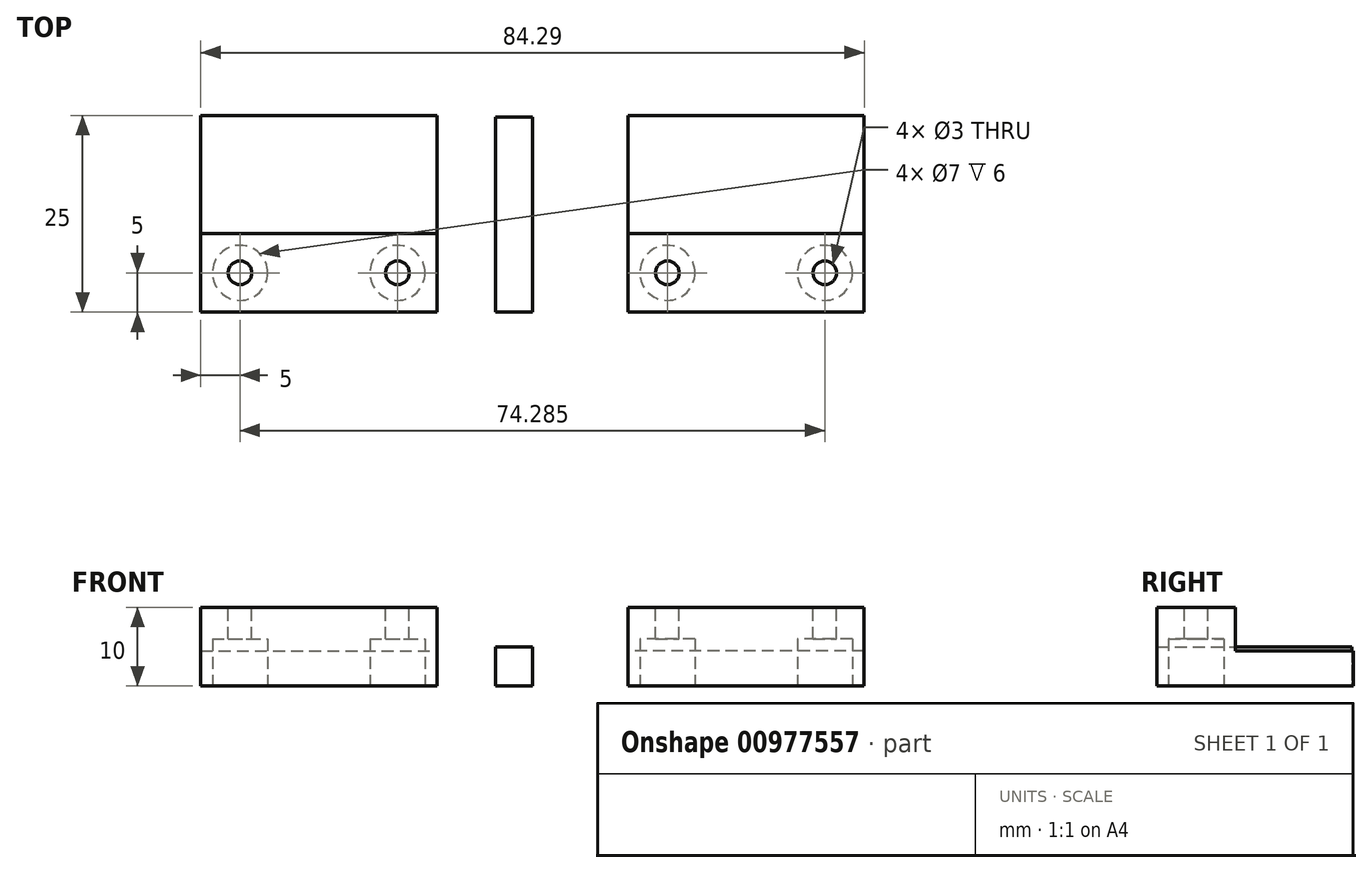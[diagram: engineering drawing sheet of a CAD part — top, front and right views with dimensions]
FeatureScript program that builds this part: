
annotation { "Feature Type Name" : "Feature", "Feature Type Description" : "" }
export const myFeature = defineFeature(function(context is Context, id is Id, definition is map)
    precondition{}
    {
        {
            var Q0;
            Q0=qCreatedBy(makeId("Top.planeOp"),FACE);
            var sketch = newSketch(context, id + "F0", { "sketchPlane" : qUnion([Q0])});
            skLineSegment(sketch, "E0.bottom", {"start": v(-15, -12.5) * mm, "end": v(15, -12.5) * mm});
            skLineSegment(sketch, "E0.top", {"start": v(-15, 12.5) * mm, "end": v(15, 12.5) * mm});
            skLineSegment(sketch, "E0.left", {"start": v(-15, -12.5) * mm, "end": v(-15, 12.5) * mm});
            skLineSegment(sketch, "E0.right", {"start": v(15, -12.5) * mm, "end": v(15, 12.5) * mm});
            skPoint(sketch, "E0.middle", {"position": v(0, 0) * mm});
            skSolve(sketch);
        }
        {
            var Q0;
            Q0=qSketchRegion(id+"F0",true);
            extrude(context, id + "F1", {"entities" : qUnion([Q0]), "depth" : 10 * mm, "offsetDistance" : 25 * mm});
        }
        {
            var Q0;
            Q0=makeQuery(id+"F1.opExtrude","CAP_FACE",FACE,{"disambiguationData":[OSD([sQuery(id+"F0.wireOp",EDGE,"E0.bottom"),sQuery(id+"F0.wireOp",EDGE,"E0.top"),sQuery(id+"F0.wireOp",EDGE,"E0.left"),sQuery(id+"F0.wireOp",EDGE,"E0.right")])],"isStart":false});
            var sketch = newSketch(context, id + "F2", { "sketchPlane" : qUnion([Q0])});
            skLineSegment(sketch, "E1.bottom", {"start": v(15, 12.5) * mm, "end": v(-15, 12.5) * mm});
            skLineSegment(sketch, "E1.top", {"start": v(15, -2.5) * mm, "end": v(-15, -2.5) * mm});
            skLineSegment(sketch, "E1.left", {"start": v(15, 12.5) * mm, "end": v(15, -2.5) * mm});
            skLineSegment(sketch, "E1.right", {"start": v(-15, 12.5) * mm, "end": v(-15, -2.5) * mm});
            skSolve(sketch);
        }
        {
            var Q0;
            Q0=makeQuery(id+"F2.imprint","IMPRINT",FACE,{"disambiguationData":[TD([[makeQuery(id+"F2.imprint","IMPRINT",EDGE,{"derivedFrom":sQuery(id+"F2.wireOp",EDGE,"E1.bottom")}),-1.0]])]});
            extrude(context, id + "F3", {"entities" : qUnion([Q0]), "operationType" : NewBodyOperationType.REMOVE, "oppositeDirection" : true, "depth" : 5.5 * mm, "offsetDistance" : 25 * mm});
        }
        {
            var Q0;
            Q0=makeQuery(id+"F1.opExtrude","CAP_FACE",FACE,{"disambiguationData":[OSD([sQuery(id+"F0.wireOp",EDGE,"E0.bottom"),sQuery(id+"F0.wireOp",EDGE,"E0.top"),sQuery(id+"F0.wireOp",EDGE,"E0.left"),sQuery(id+"F0.wireOp",EDGE,"E0.right")])],"isStart":false});
            var sketch = newSketch(context, id + "F4", { "sketchPlane" : qUnion([Q0])});
            skLineSegment(sketch, "E2", {"start": v(15, -7.5) * mm, "end": v(10, -7.5) * mm, "construction": true});
            skCircle(sketch, "E3", {"center": v(10, -7.5) * mm, "radius": 1.5 * mm});
            skCircle(sketch, "E4", {"center": v(-10, -7.5) * mm, "radius": 1.5 * mm});
            skSolve(sketch);
        }
        {
            var Q0;
            Q0=qSketchRegion(id+"F4",true);
            extrude(context, id + "F5", {"entities" : qUnion([Q0]), "operationType" : NewBodyOperationType.REMOVE, "oppositeDirection" : true, "depth" : 25 * mm, "offsetDistance" : 25 * mm});
        }
        {
            var Q0;
            Q0=makeQuery(id+"F1.opExtrude","CAP_FACE",FACE,{"disambiguationData":[OSD([sQuery(id+"F0.wireOp",EDGE,"E0.bottom"),sQuery(id+"F0.wireOp",EDGE,"E0.top"),sQuery(id+"F0.wireOp",EDGE,"E0.left"),sQuery(id+"F0.wireOp",EDGE,"E0.right")])],"isStart":true});
            var sketch = newSketch(context, id + "F6", { "sketchPlane" : qUnion([Q0])});
            skCircle(sketch, "E5", {"center": v(10, 7.5) * mm, "radius": 3.5 * mm});
            skCircle(sketch, "E6", {"center": v(-10, 7.5) * mm, "radius": 3.5 * mm});
            skSolve(sketch);
        }
        {
            var Q0;
            Q0=qSketchRegion(id+"F6",true);
            extrude(context, id + "F7", {"entities" : qUnion([Q0]), "operationType" : NewBodyOperationType.REMOVE, "oppositeDirection" : true, "depth" : 6 * mm, "offsetDistance" : 25 * mm});
        }
        {
            var Q0;
            Q0=makeQuery(id+"F1.opExtrude","CAP_FACE",FACE,{"disambiguationData":[OSD([sQuery(id+"F0.wireOp",EDGE,"E0.bottom"),sQuery(id+"F0.wireOp",EDGE,"E0.top"),sQuery(id+"F0.wireOp",EDGE,"E0.left"),sQuery(id+"F0.wireOp",EDGE,"E0.right")])],"isStart":true});
            var sketch = newSketch(context, id + "F8", { "sketchPlane" : qUnion([Q0])});
            skLineSegment(sketch, "E7", {"start": v(15, 0) * mm, "end": v(22.48, 0) * mm});
            skLineSegment(sketch, "E8", {"start": v(22.48, 0) * mm, "end": v(22.48, 12.5) * mm});
            skLineSegment(sketch, "E9.bottom", {"start": v(22.48, 12.5) * mm, "end": v(27.14, 12.5) * mm});
            skLineSegment(sketch, "E9.top", {"start": v(22.48, -12.26) * mm, "end": v(27.14, -12.26) * mm});
            skLineSegment(sketch, "E9.left", {"start": v(22.48, 12.5) * mm, "end": v(22.48, -12.26) * mm});
            skLineSegment(sketch, "E9.right", {"start": v(27.14, 12.5) * mm, "end": v(27.14, -12.26) * mm});
            skSolve(sketch);
        }
        {
            var Q0;
            Q0=qSketchRegion(id+"F8",true);
            extrude(context, id + "F9", {"entities" : qUnion([Q0]), "depth" : -5 * mm, "offsetDistance" : 25 * mm});
        }
        {
            var Q0;
            Q0=makeQuery(id+"F1.opExtrude","SWEPT_BODY",BODY,{"disambiguationData":[OSD([sQuery(id+"F0.wireOp",EDGE,"E0.bottom"),sQuery(id+"F0.wireOp",EDGE,"E0.top"),sQuery(id+"F0.wireOp",EDGE,"E0.left"),sQuery(id+"F0.wireOp",EDGE,"E0.right")])]});
            var Q1;
            Q1=makeQuery(id+"F9.opExtrude","SWEPT_FACE",FACE,{"disambiguationData":[OSD([sQuery(id+"F8.wireOp",EDGE,"E9.right")])]});
            mirror(context, id + "F10", {"entities" : qUnion([Q0]), "mirrorPlane" : qUnion([Q1])});
        }
    });
